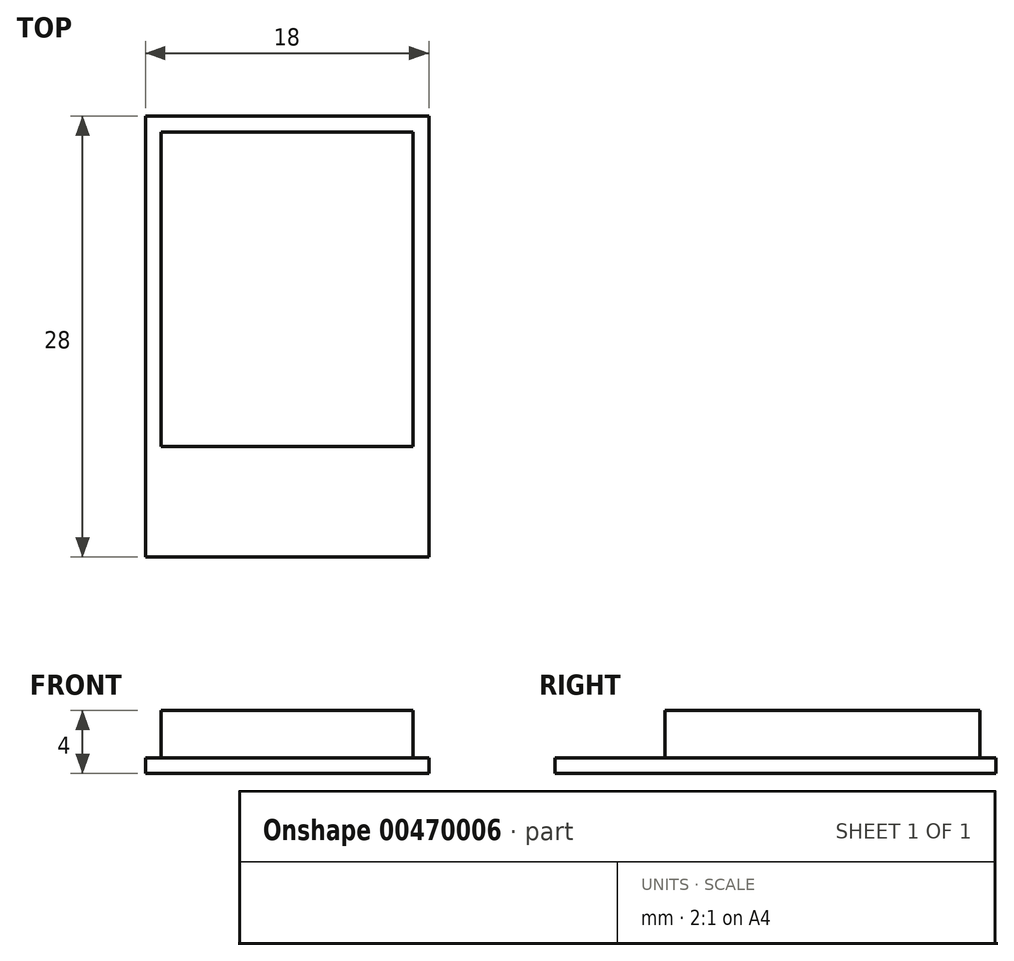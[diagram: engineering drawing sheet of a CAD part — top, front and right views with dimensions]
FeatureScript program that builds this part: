
annotation { "Feature Type Name" : "Feature", "Feature Type Description" : "" }
export const myFeature = defineFeature(function(context is Context, id is Id, definition is map)
    precondition{}
    {
        {
            var Q0;
            Q0=qCreatedBy(makeId("Top.planeOp"),FACE);
            var sketch = newSketch(context, id + "F0", { "sketchPlane" : qUnion([Q0])});
            skLineSegment(sketch, "E0.bottom", {"start": v(9, -14) * mm, "end": v(-9, -14) * mm});
            skLineSegment(sketch, "E0.top", {"start": v(9, 14) * mm, "end": v(-9, 14) * mm});
            skLineSegment(sketch, "E0.left", {"start": v(9, -14) * mm, "end": v(9, 14) * mm});
            skLineSegment(sketch, "E0.right", {"start": v(-9, -14) * mm, "end": v(-9, 14) * mm});
            skPoint(sketch, "E0.middle", {"position": v(0, 0) * mm});
            skLineSegment(sketch, "E1.bottom", {"start": v(8, -7) * mm, "end": v(-8, -7) * mm});
            skLineSegment(sketch, "E1.top", {"start": v(8, 13) * mm, "end": v(-8, 13) * mm});
            skLineSegment(sketch, "E1.left", {"start": v(8, -7) * mm, "end": v(8, 13) * mm});
            skLineSegment(sketch, "E1.right", {"start": v(-8, -7) * mm, "end": v(-8, 13) * mm});
            skPoint(sketch, "E1.middle", {"position": v(0, 3) * mm});
            skSolve(sketch);
        }
        {
            var Q0;
            Q0=makeQuery(id+"F0.imprint","IMPRINT",FACE,{"disambiguationData":[TD([[makeQuery(id+"F0.imprint","IMPRINT",EDGE,{"derivedFrom":sQuery(id+"F0.wireOp",EDGE,"E1.bottom")}),-1.0]])]});
            extrude(context, id + "F1", {"entities" : qUnion([Q0]), "depth" : 4 * mm, "offsetDistance" : 25 * mm});
        }
        {
            var Q0;
            Q0 = qSketchRegion(id + "F0", true);
            extrude(context, id + "F2", {"entities" : qUnion([Q0]), "operationType" : NewBodyOperationType.ADD, "depth" : 1 * mm, "offsetDistance" : 25 * mm});
        }
    });
